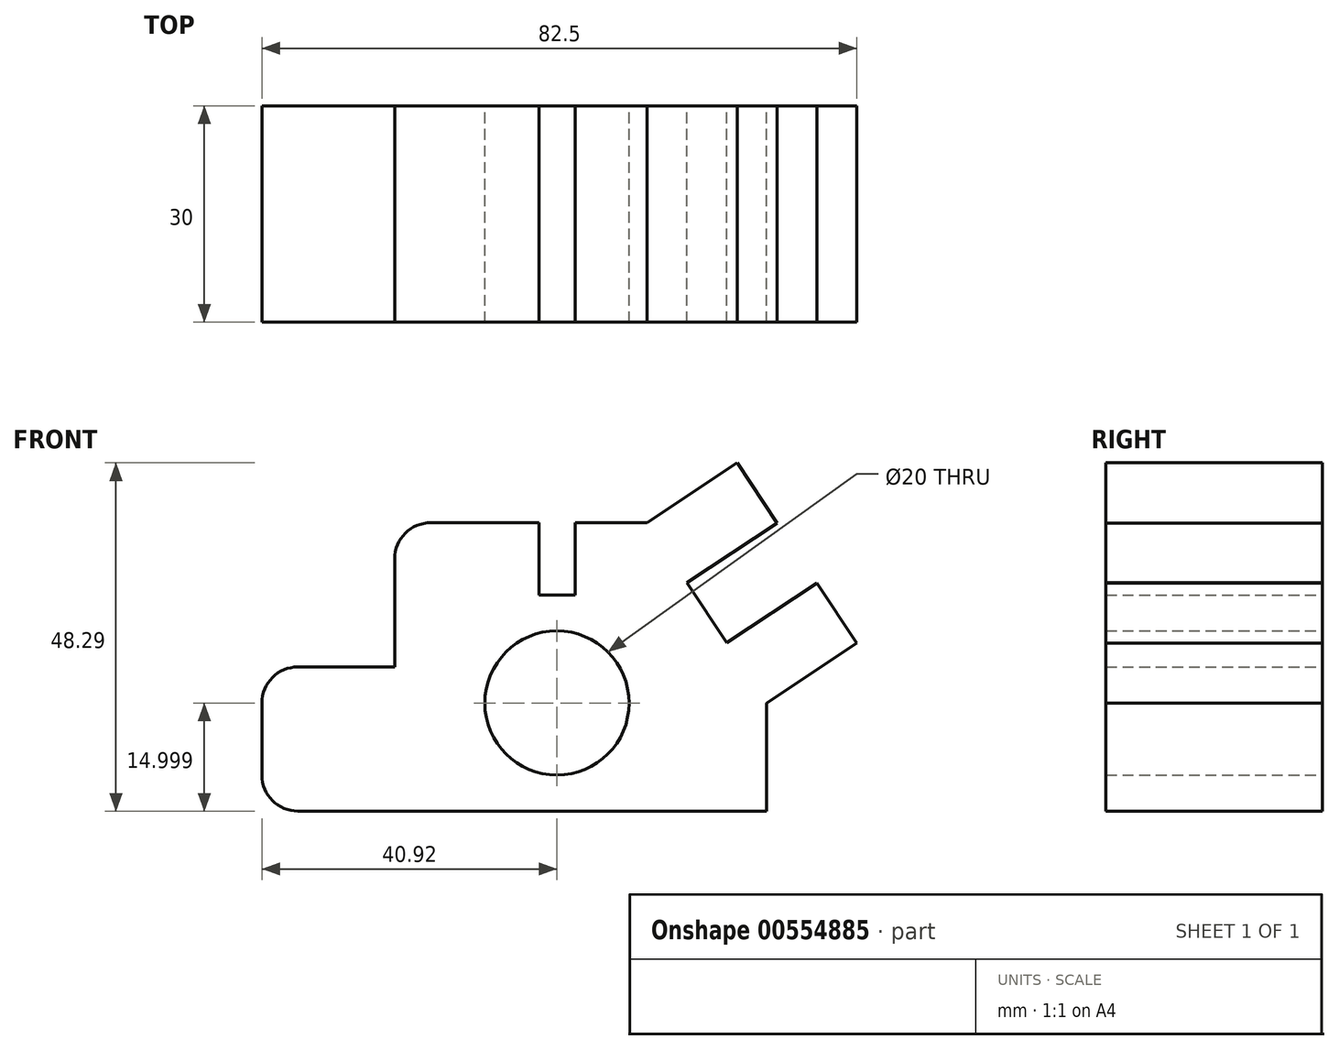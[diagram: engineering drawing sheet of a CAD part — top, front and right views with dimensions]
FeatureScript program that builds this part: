
annotation { "Feature Type Name" : "Feature", "Feature Type Description" : "" }
export const myFeature = defineFeature(function(context is Context, id is Id, definition is map)
    precondition{}
    {
        {
            var Q0;
            Q0=qCreatedBy(makeId("Front.planeOp"),FACE);
            var sketch = newSketch(context, id + "F0", { "sketchPlane" : qUnion([Q0])});
            skLineSegment(sketch, "E0", {"start": v(15, 32.95) * mm, "end": v(5, 32.95) * mm});
            skLineSegment(sketch, "E1", {"start": v(5, 32.95) * mm, "end": v(5, 22.95) * mm});
            skLineSegment(sketch, "E2", {"start": v(5, 22.95) * mm, "end": v(0, 22.95) * mm});
            skLineSegment(sketch, "E3", {"start": v(0, 22.95) * mm, "end": v(0, 32.95) * mm});
            skLineSegment(sketch, "E4", {"start": v(0, 32.95) * mm, "end": v(-15, 32.95) * mm});
            skLineSegment(sketch, "E5", {"start": v(-20, 27.95) * mm, "end": v(-20, 12.95) * mm});
            skLineSegment(sketch, "E6", {"start": v(-20, 12.95) * mm, "end": v(-33.42, 12.95) * mm});
            skLineSegment(sketch, "E7", {"start": v(-38.42, 7.95) * mm, "end": v(-38.42, -2.05) * mm});
            skLineSegment(sketch, "E8", {"start": v(-33.42, -7.05) * mm, "end": v(31.58, -7.05) * mm});
            skLineSegment(sketch, "E9", {"start": v(31.58, -7.05) * mm, "end": v(31.58, 7.95) * mm});
            skPoint(sketch, "E10", {"position": v(23.3, 20.45) * mm});
            skLineSegment(sketch, "E11", {"start": v(20.53, 24.62) * mm, "end": v(26.06, 16.28) * mm});
            skLineSegment(sketch, "E12", {"start": v(23.3, 20.45) * mm, "end": v(26.06, 16.28) * mm});
            skLineSegment(sketch, "E13", {"start": v(23.3, 20.45) * mm, "end": v(20.53, 24.62) * mm});
            skLineSegment(sketch, "E14", {"start": v(20.53, 24.62) * mm, "end": v(33.03, 32.9) * mm});
            skLineSegment(sketch, "E15", {"start": v(26.06, 16.28) * mm, "end": v(38.56, 24.57) * mm});
            skLineSegment(sketch, "E16", {"start": v(38.56, 24.57) * mm, "end": v(44.08, 16.24) * mm});
            skLineSegment(sketch, "E17", {"start": v(44.08, 16.24) * mm, "end": v(31.58, 7.95) * mm});
            skLineSegment(sketch, "E18", {"start": v(33.03, 32.9) * mm, "end": v(27.5, 41.24) * mm});
            skLineSegment(sketch, "E19", {"start": v(27.5, 41.24) * mm, "end": v(15, 32.95) * mm});
            skPoint(sketch, "E20.visualSharp", {"position": v(-20, 32.95) * mm});
            skArc(sketch, "E20.filletArc", {"start": v(-15, 32.95) * mm, "mid": v(-18.54, 31.48) * mm, "end": v(-20, 27.95) * mm});
            skPoint(sketch, "E21.visualSharp", {"position": v(-38.42, 12.95) * mm});
            skArc(sketch, "E21.filletArc", {"start": v(-33.42, 12.95) * mm, "mid": v(-36.95, 11.48) * mm, "end": v(-38.42, 7.95) * mm});
            skPoint(sketch, "E22.visualSharp", {"position": v(-38.42, -7.05) * mm});
            skArc(sketch, "E22.filletArc", {"start": v(-38.42, -2.05) * mm, "mid": v(-36.95, -5.59) * mm, "end": v(-33.42, -7.05) * mm});
            skCircle(sketch, "E23", {"center": v(2.5, 7.95) * mm, "radius": 10 * mm});
            skPoint(sketch, "E23.centerSnap0", {"position": v(2.5, 22.95) * mm});
            skSolve(sketch);
        }
        {
            var Q0;
            Q0 = qSketchRegion(id + "F0", true);
            extrude(context, id + "F1", {"entities" : qUnion([Q0]), "depth" : 30 * mm, "offsetDistance" : 25 * mm});
        }
    });
